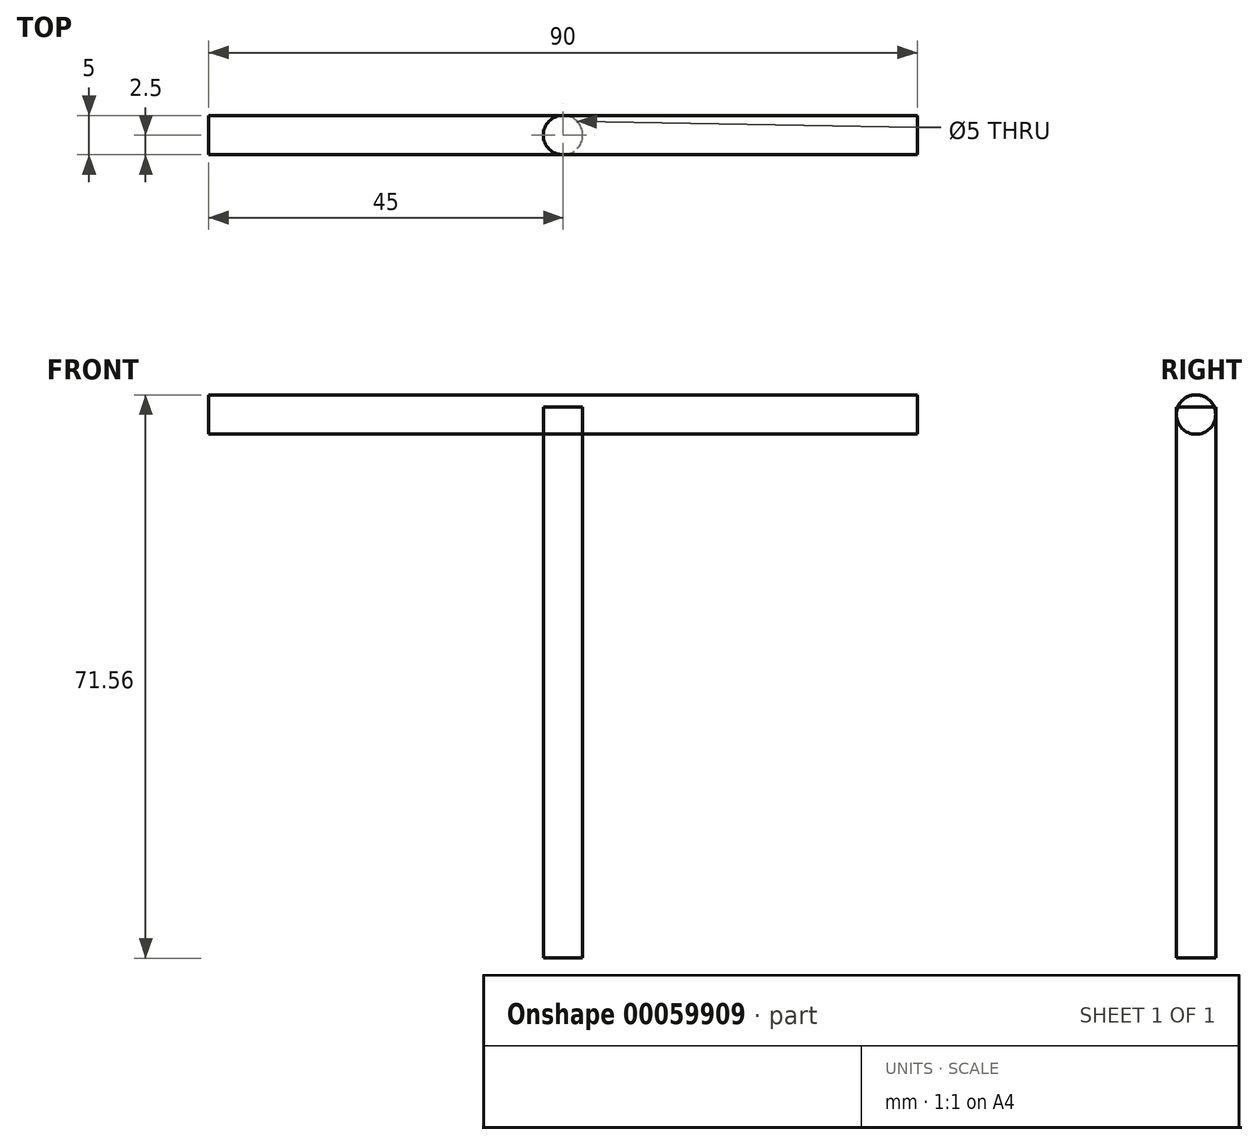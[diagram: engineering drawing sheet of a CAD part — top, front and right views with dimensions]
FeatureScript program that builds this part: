
annotation { "Feature Type Name" : "Feature", "Feature Type Description" : "" }
export const myFeature = defineFeature(function(context is Context, id is Id, definition is map)
    precondition{}
    {
        {
            var Q0;
            Q0=qCreatedBy(makeId("Front.planeOp"),FACE);
            var sketch = newSketch(context, id + "F0", { "sketchPlane" : qUnion([Q0])});
            skLineSegment(sketch, "E0", {"start": v(0, -37.54) * mm, "end": v(0, 37.46) * mm});
            skLineSegment(sketch, "E1", {"start": v(0, 37.46) * mm, "end": v(-45, 37.46) * mm});
            skLineSegment(sketch, "E2.MirrorCS", {"start": v(0, 37.46) * mm, "end": v(45, 37.46) * mm});
            skLineSegment(sketch, "E3", {"start": v(-45, 39.96) * mm, "end": v(45, 39.96) * mm});
            skLineSegment(sketch, "E4", {"start": v(-2.5, -37.54) * mm, "end": v(-2.5, 39.96) * mm});
            skSolve(sketch);
        }
        {
            var Q0;
            Q0=sQuery(id+"F0.wireOp",EDGE,"E3");
            var Q1;
            Q1=sQuery(id+"F0.wireOp",EDGE,"E1");
            revolve(context, id + "F1", {"bodyType" : ToolBodyType.SURFACE, "surfaceEntities" : qUnion([Q0]), "axis" : qUnion([Q1]), "revolveType" : RevolveType.FULL});
        }
        {
            var Q0;
            Q0=qCreatedBy(makeId("Front.planeOp"),FACE);
            var sketch = newSketch(context, id + "F2", { "sketchPlane" : qUnion([Q0])});
            skLineSegment(sketch, "E5", {"start": v(0, 38.4) * mm, "end": v(0, -31.6) * mm});
            skLineSegment(sketch, "E6", {"start": v(-2.5, 38.4) * mm, "end": v(-2.5, -31.6) * mm});
            skSolve(sketch);
        }
        {
            var Q0;
            Q0=sQuery(id+"F2.wireOp",EDGE,"E6");
            var Q1;
            Q1=sQuery(id+"F2.wireOp",EDGE,"E5");
            revolve(context, id + "F3", {"bodyType" : ToolBodyType.SURFACE, "surfaceEntities" : qUnion([Q0]), "axis" : qUnion([Q1]), "revolveType" : RevolveType.FULL});
        }
    });
